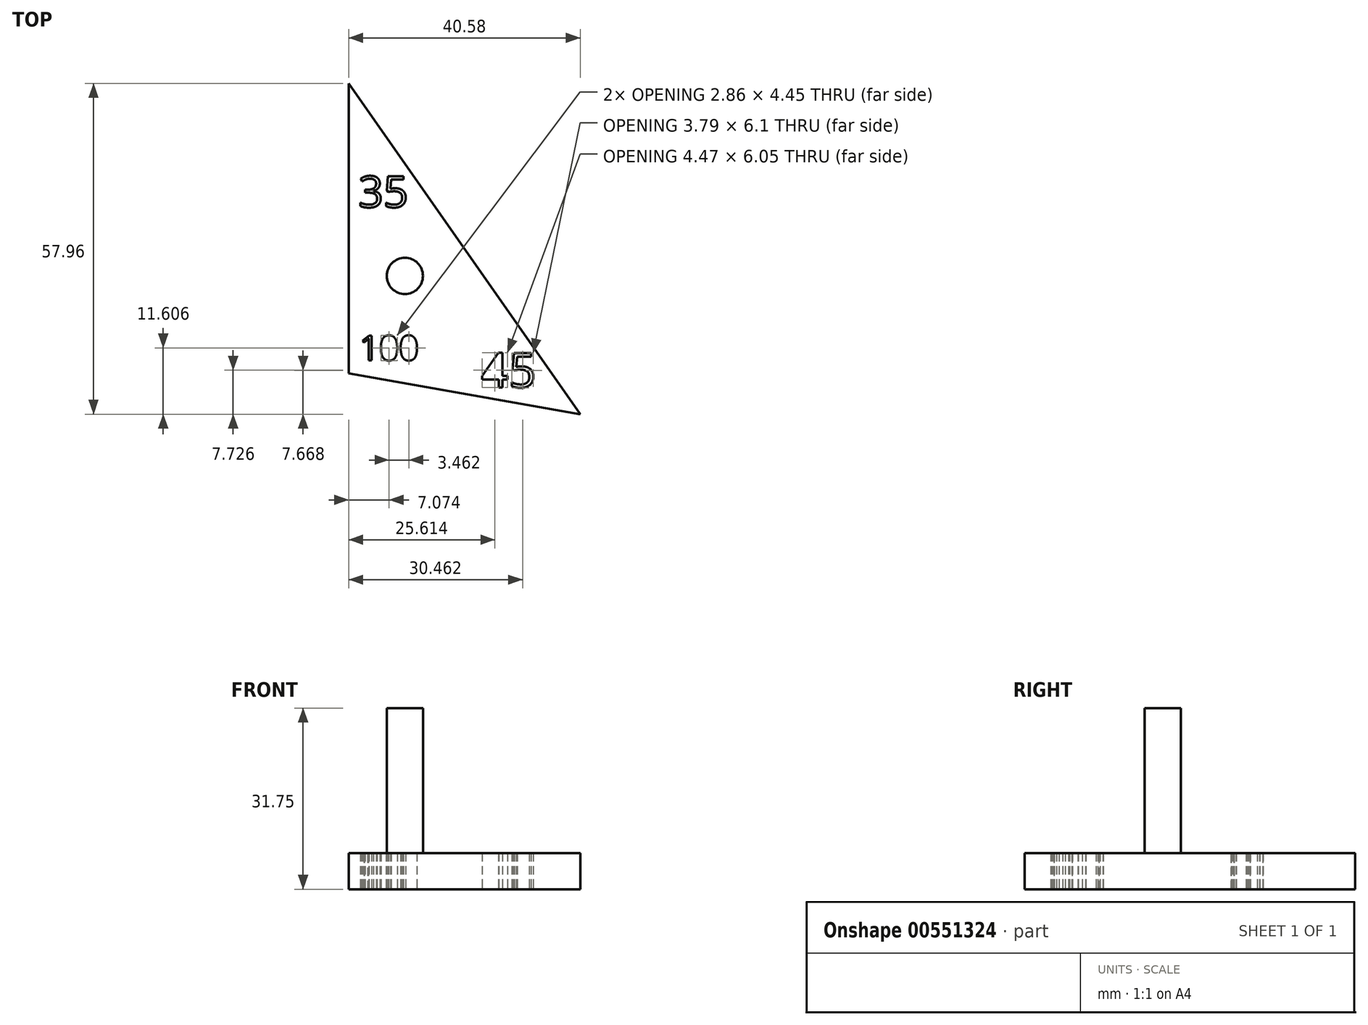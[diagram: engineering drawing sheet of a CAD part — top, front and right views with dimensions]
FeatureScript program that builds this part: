
annotation { "Feature Type Name" : "Feature", "Feature Type Description" : "" }
export const myFeature = defineFeature(function(context is Context, id is Id, definition is map)
    precondition{}
    {
        {
            var Q0;
            Q0=qCreatedBy(makeId("Top.planeOp"),FACE);
            var sketch = newSketch(context, id + "F0", { "sketchPlane" : qUnion([Q0])});
            skLineSegment(sketch, "E0", {"start": v(0, 0) * mm, "end": v(0, 50.8) * mm});
            skLineSegment(sketch, "E1", {"start": v(0, 50.8) * mm, "end": v(40.58, -7.16) * mm});
            skLineSegment(sketch, "E2", {"start": v(40.58, -7.16) * mm, "end": v(0, 0) * mm});
            skText(sketch, "E3", { "text": "100", "fontName": "OpenSans-Regular.ttf"});
            skText(sketch, "E4", { "text": "35", "fontName": "OpenSans-Regular.ttf"});
            skText(sketch, "E5", { "text": "45", "fontName": "OpenSans-Regular.ttf"});
            const initialGuessF0  = {"E3": [0.00188, 0.00228, 1, 0, 0.00436], "E4": [0.0017, 0.0291, 1, 0, 0.0055], "E5": [0.0232, -0.00246, 1, 0, 0.00607]};
            skSetInitialGuess(sketch, initialGuessF0);
            skSolve(sketch);
        }
        {
            var Q0;
            Q0=makeQuery(id+"F0.imprint","IMPRINT",FACE,{"disambiguationData":[TD([[makeQuery(id+"F0.imprint","IMPRINT",EDGE,{"derivedFrom":sQuery(id+"F0.wireOp",EDGE,"E0")}),-1.0]])]});
            extrude(context, id + "F1", {"entities" : qUnion([Q0]), "depth" : 6.35 * mm, "offsetDistance" : 25.4 * mm});
        }
        {
            var Q0;
            Q0=makeQuery(id+"F1.opExtrude","CAP_FACE",FACE,{"disambiguationData":[OSD([sQuery(id+"F0.wireOp",EDGE,"E0"),sQuery(id+"F0.wireOp",EDGE,"E1"),sQuery(id+"F0.wireOp",EDGE,"E2"),sQuery(id+"F0.wireOp",EDGE,"E3.sketch_text.stroke-0"),sQuery(id+"F0.wireOp",EDGE,"E3.sketch_text.stroke-1"),sQuery(id+"F0.wireOp",EDGE,"E3.sketch_text.stroke-2"),sQuery(id+"F0.wireOp",EDGE,"E3.sketch_text.stroke-3"),sQuery(id+"F0.wireOp",EDGE,"E3.sketch_text.stroke-4"),sQuery(id+"F0.wireOp",EDGE,"E3.sketch_text.stroke-5"),sQuery(id+"F0.wireOp",EDGE,"E3.sketch_text.stroke-6"),sQuery(id+"F0.wireOp",EDGE,"E3.sketch_text.stroke-7"),sQuery(id+"F0.wireOp",EDGE,"E3.sketch_text.stroke-8"),sQuery(id+"F0.wireOp",EDGE,"E3.sketch_text.stroke-9"),sQuery(id+"F0.wireOp",EDGE,"E3.sketch_text.stroke-10"),sQuery(id+"F0.wireOp",EDGE,"E3.sketch_text.stroke-11"),sQuery(id+"F0.wireOp",EDGE,"E3.sketch_text.stroke-12"),sQuery(id+"F0.wireOp",EDGE,"E3.sketch_text.stroke-13"),sQuery(id+"F0.wireOp",EDGE,"E3.sketch_text.stroke-14"),sQuery(id+"F0.wireOp",EDGE,"E3.sketch_text.stroke-15"),sQuery(id+"F0.wireOp",EDGE,"E3.sketch_text.stroke-16"),sQuery(id+"F0.wireOp",EDGE,"E3.sketch_text.stroke-25"),sQuery(id+"F0.wireOp",EDGE,"E3.sketch_text.stroke-26"),sQuery(id+"F0.wireOp",EDGE,"E3.sketch_text.stroke-27"),sQuery(id+"F0.wireOp",EDGE,"E3.sketch_text.stroke-28"),sQuery(id+"F0.wireOp",EDGE,"E3.sketch_text.stroke-29"),sQuery(id+"F0.wireOp",EDGE,"E3.sketch_text.stroke-30"),sQuery(id+"F0.wireOp",EDGE,"E3.sketch_text.stroke-31"),sQuery(id+"F0.wireOp",EDGE,"E3.sketch_text.stroke-32"),sQuery(id+"F0.wireOp",EDGE,"E4.sketch_text.stroke-0"),sQuery(id+"F0.wireOp",EDGE,"E4.sketch_text.stroke-1"),sQuery(id+"F0.wireOp",EDGE,"E4.sketch_text.stroke-2"),sQuery(id+"F0.wireOp",EDGE,"E4.sketch_text.stroke-3"),sQuery(id+"F0.wireOp",EDGE,"E4.sketch_text.stroke-4"),sQuery(id+"F0.wireOp",EDGE,"E4.sketch_text.stroke-5"),sQuery(id+"F0.wireOp",EDGE,"E4.sketch_text.stroke-6"),sQuery(id+"F0.wireOp",EDGE,"E4.sketch_text.stroke-7"),sQuery(id+"F0.wireOp",EDGE,"E4.sketch_text.stroke-8"),sQuery(id+"F0.wireOp",EDGE,"E4.sketch_text.stroke-9"),sQuery(id+"F0.wireOp",EDGE,"E4.sketch_text.stroke-10"),sQuery(id+"F0.wireOp",EDGE,"E4.sketch_text.stroke-11"),sQuery(id+"F0.wireOp",EDGE,"E4.sketch_text.stroke-12"),sQuery(id+"F0.wireOp",EDGE,"E4.sketch_text.stroke-13"),sQuery(id+"F0.wireOp",EDGE,"E4.sketch_text.stroke-14"),sQuery(id+"F0.wireOp",EDGE,"E4.sketch_text.stroke-15"),sQuery(id+"F0.wireOp",EDGE,"E4.sketch_text.stroke-16"),sQuery(id+"F0.wireOp",EDGE,"E4.sketch_text.stroke-17"),sQuery(id+"F0.wireOp",EDGE,"E4.sketch_text.stroke-18"),sQuery(id+"F0.wireOp",EDGE,"E4.sketch_text.stroke-19"),sQuery(id+"F0.wireOp",EDGE,"E4.sketch_text.stroke-20"),sQuery(id+"F0.wireOp",EDGE,"E4.sketch_text.stroke-21"),sQuery(id+"F0.wireOp",EDGE,"E4.sketch_text.stroke-22"),sQuery(id+"F0.wireOp",EDGE,"E4.sketch_text.stroke-23"),sQuery(id+"F0.wireOp",EDGE,"E4.sketch_text.stroke-24"),sQuery(id+"F0.wireOp",EDGE,"E4.sketch_text.stroke-25"),sQuery(id+"F0.wireOp",EDGE,"E4.sketch_text.stroke-26"),sQuery(id+"F0.wireOp",EDGE,"E4.sketch_text.stroke-27"),sQuery(id+"F0.wireOp",EDGE,"E4.sketch_text.stroke-28"),sQuery(id+"F0.wireOp",EDGE,"E4.sketch_text.stroke-29"),sQuery(id+"F0.wireOp",EDGE,"E4.sketch_text.stroke-30"),sQuery(id+"F0.wireOp",EDGE,"E4.sketch_text.stroke-31"),sQuery(id+"F0.wireOp",EDGE,"E4.sketch_text.stroke-32"),sQuery(id+"F0.wireOp",EDGE,"E4.sketch_text.stroke-33"),sQuery(id+"F0.wireOp",EDGE,"E4.sketch_text.stroke-34"),sQuery(id+"F0.wireOp",EDGE,"E4.sketch_text.stroke-35"),sQuery(id+"F0.wireOp",EDGE,"E4.sketch_text.stroke-36"),sQuery(id+"F0.wireOp",EDGE,"E4.sketch_text.stroke-37"),sQuery(id+"F0.wireOp",EDGE,"E4.sketch_text.stroke-38"),sQuery(id+"F0.wireOp",EDGE,"E4.sketch_text.stroke-39"),sQuery(id+"F0.wireOp",EDGE,"E4.sketch_text.stroke-40"),sQuery(id+"F0.wireOp",EDGE,"E4.sketch_text.stroke-41"),sQuery(id+"F0.wireOp",EDGE,"E4.sketch_text.stroke-42"),sQuery(id+"F0.wireOp",EDGE,"E4.sketch_text.stroke-43"),sQuery(id+"F0.wireOp",EDGE,"E4.sketch_text.stroke-44"),sQuery(id+"F0.wireOp",EDGE,"E4.sketch_text.stroke-45"),sQuery(id+"F0.wireOp",EDGE,"E4.sketch_text.stroke-46"),sQuery(id+"F0.wireOp",EDGE,"E5.sketch_text.stroke-0"),sQuery(id+"F0.wireOp",EDGE,"E5.sketch_text.stroke-1"),sQuery(id+"F0.wireOp",EDGE,"E5.sketch_text.stroke-2"),sQuery(id+"F0.wireOp",EDGE,"E5.sketch_text.stroke-3"),sQuery(id+"F0.wireOp",EDGE,"E5.sketch_text.stroke-4"),sQuery(id+"F0.wireOp",EDGE,"E5.sketch_text.stroke-5"),sQuery(id+"F0.wireOp",EDGE,"E5.sketch_text.stroke-6"),sQuery(id+"F0.wireOp",EDGE,"E5.sketch_text.stroke-7"),sQuery(id+"F0.wireOp",EDGE,"E5.sketch_text.stroke-8"),sQuery(id+"F0.wireOp",EDGE,"E5.sketch_text.stroke-9"),sQuery(id+"F0.wireOp",EDGE,"E5.sketch_text.stroke-10"),sQuery(id+"F0.wireOp",EDGE,"E5.sketch_text.stroke-17"),sQuery(id+"F0.wireOp",EDGE,"E5.sketch_text.stroke-18"),sQuery(id+"F0.wireOp",EDGE,"E5.sketch_text.stroke-19"),sQuery(id+"F0.wireOp",EDGE,"E5.sketch_text.stroke-20"),sQuery(id+"F0.wireOp",EDGE,"E5.sketch_text.stroke-21"),sQuery(id+"F0.wireOp",EDGE,"E5.sketch_text.stroke-22"),sQuery(id+"F0.wireOp",EDGE,"E5.sketch_text.stroke-23"),sQuery(id+"F0.wireOp",EDGE,"E5.sketch_text.stroke-24"),sQuery(id+"F0.wireOp",EDGE,"E5.sketch_text.stroke-25"),sQuery(id+"F0.wireOp",EDGE,"E5.sketch_text.stroke-26"),sQuery(id+"F0.wireOp",EDGE,"E5.sketch_text.stroke-27"),sQuery(id+"F0.wireOp",EDGE,"E5.sketch_text.stroke-28"),sQuery(id+"F0.wireOp",EDGE,"E5.sketch_text.stroke-29"),sQuery(id+"F0.wireOp",EDGE,"E5.sketch_text.stroke-30"),sQuery(id+"F0.wireOp",EDGE,"E5.sketch_text.stroke-31"),sQuery(id+"F0.wireOp",EDGE,"E5.sketch_text.stroke-32"),sQuery(id+"F0.wireOp",EDGE,"E5.sketch_text.stroke-33"),sQuery(id+"F0.wireOp",EDGE,"E5.sketch_text.stroke-34"),sQuery(id+"F0.wireOp",EDGE,"E5.sketch_text.stroke-35")])],"isStart":false});
            var sketch = newSketch(context, id + "F2", { "sketchPlane" : qUnion([Q0])});
            skCircle(sketch, "E6", {"center": v(9.84, 17.07) * mm, "radius": 3.18 * mm});
            skSolve(sketch);
        }
        {
            var Q0;
            Q0=makeQuery(id+"F2.imprint","IMPRINT",FACE,{"disambiguationData":[TD([[makeQuery(id+"F2.imprint","IMPRINT",EDGE,{"derivedFrom":sQuery(id+"F2.wireOp",EDGE,"E6")}),1.0]])]});
            extrude(context, id + "F3", {"entities" : qUnion([Q0]), "operationType" : NewBodyOperationType.ADD, "depth" : 25.4 * mm, "offsetDistance" : 25.4 * mm});
        }
    });
